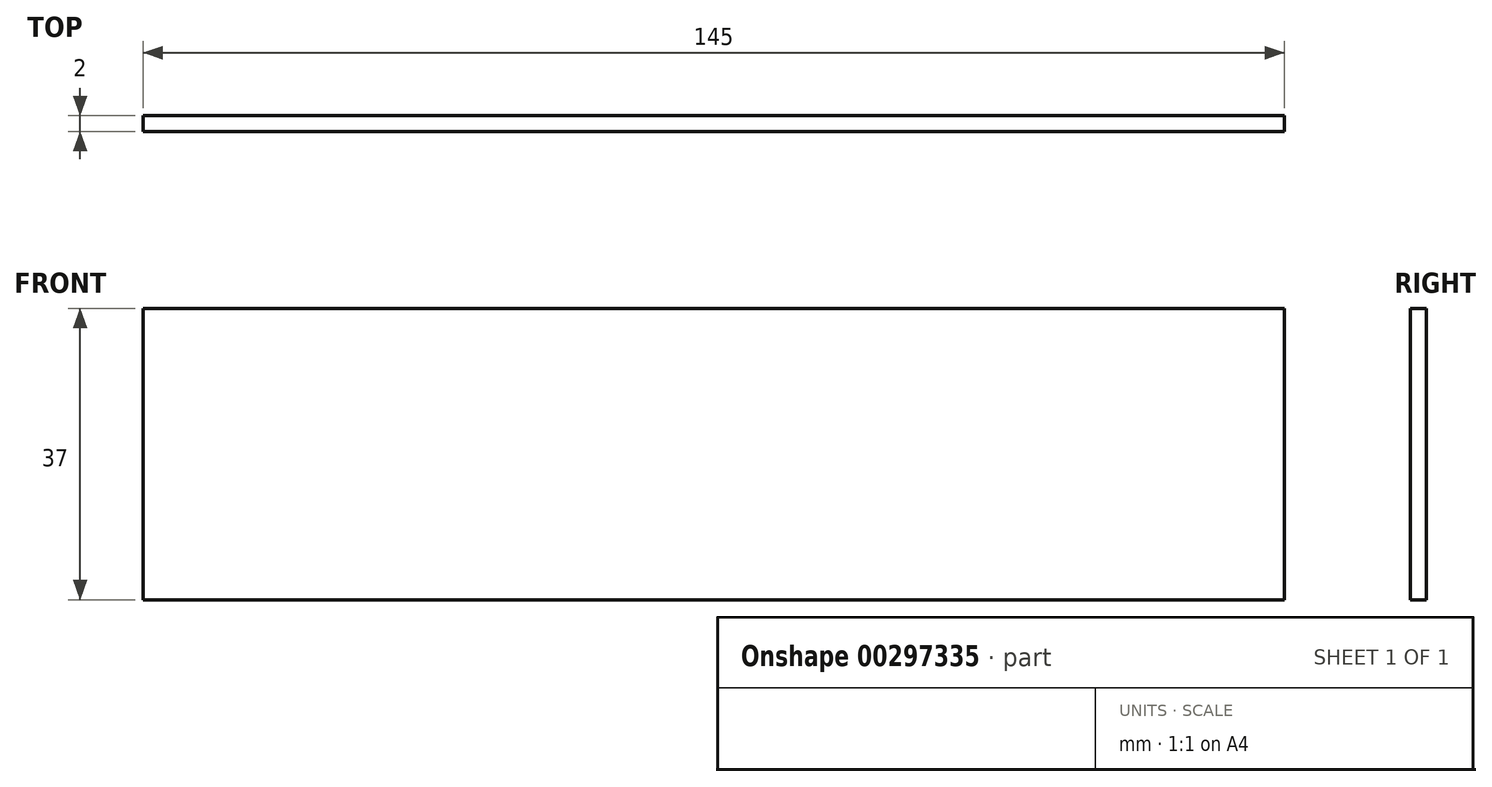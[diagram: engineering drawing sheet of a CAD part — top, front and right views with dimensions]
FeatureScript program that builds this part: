
annotation { "Feature Type Name" : "Feature", "Feature Type Description" : "" }
export const myFeature = defineFeature(function(context is Context, id is Id, definition is map)
    precondition{}
    {
        {
            var Q0;
            Q0=qCreatedBy(makeId("Front.planeOp"),FACE);
            var sketch = newSketch(context, id + "F0", { "sketchPlane" : qUnion([Q0])});
            skLineSegment(sketch, "E0.bottom", {"start": v(72.5, 17.5) * mm, "end": v(-72.5, 17.5) * mm});
            skLineSegment(sketch, "E0.top", {"start": v(72.5, -17.5) * mm, "end": v(-72.5, -17.5) * mm});
            skLineSegment(sketch, "E0.left", {"start": v(72.5, 17.5) * mm, "end": v(72.5, -17.5) * mm});
            skLineSegment(sketch, "E0.right", {"start": v(-72.5, 17.5) * mm, "end": v(-72.5, -17.5) * mm});
            skPoint(sketch, "E0.middle", {"position": v(0, 0) * mm});
            skSolve(sketch);
        }
        {
            var Q0;
            Q0=qSketchRegion(id+"F0",true);
            extrude(context, id + "F1", {"entities" : qUnion([Q0]), "depth" : 2 * mm});
        }
        {
            var Q0;
            Q0=makeQuery(id+"F1.opExtrude","SWEPT_FACE",FACE,{"disambiguationData":[OSD([sQuery(id+"F0.wireOp",EDGE,"E0.top")])]});
            var sketch = newSketch(context, id + "F2", { "sketchPlane" : qUnion([Q0])});
            skLineSegment(sketch, "E1.bottom", {"start": v(-72.5, 2) * mm, "end": v(72.5, 2) * mm});
            skLineSegment(sketch, "E1.top", {"start": v(-72.5, 0) * mm, "end": v(72.5, 0) * mm});
            skLineSegment(sketch, "E1.left", {"start": v(-72.5, 2) * mm, "end": v(-72.5, 0) * mm});
            skLineSegment(sketch, "E1.right", {"start": v(72.5, 2) * mm, "end": v(72.5, 0) * mm});
            skSolve(sketch);
        }
        {
            var Q0;
            Q0 = qSketchRegion(id + "F2", true);
            extrude(context, id + "F3", {"entities" : qUnion([Q0]), "operationType" : NewBodyOperationType.ADD, "depth" : 2 * mm});
        }
    });
